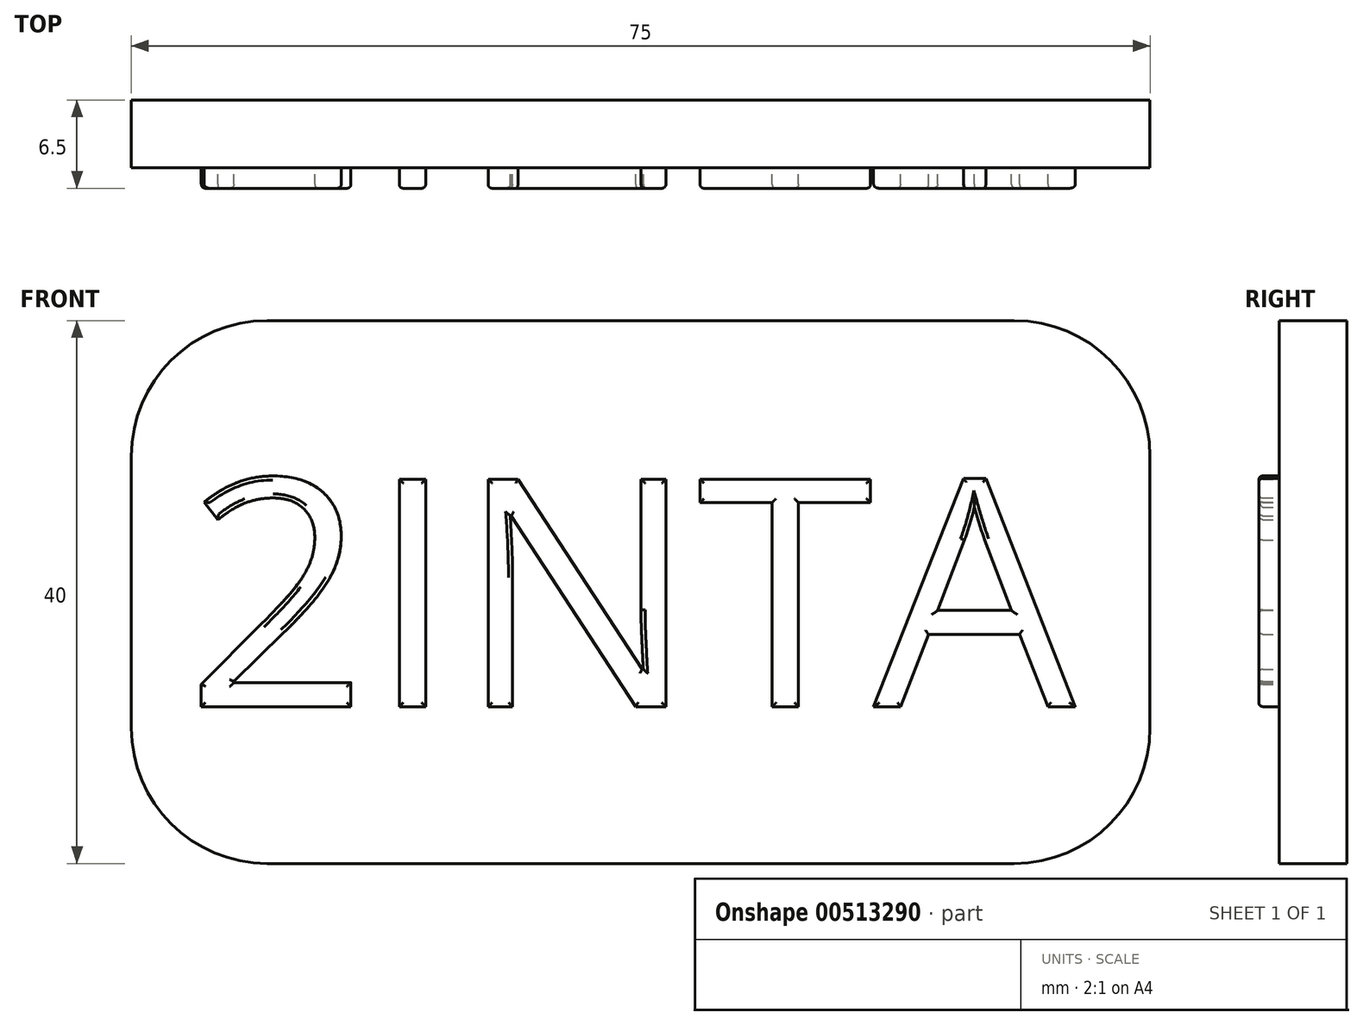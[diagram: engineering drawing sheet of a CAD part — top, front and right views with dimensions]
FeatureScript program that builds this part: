
annotation { "Feature Type Name" : "Feature", "Feature Type Description" : "" }
export const myFeature = defineFeature(function(context is Context, id is Id, definition is map)
    precondition{}
    {
        {
            var Q0;
            Q0=qCreatedBy(makeId("Front.planeOp"),FACE);
            var sketch = newSketch(context, id + "F0", { "sketchPlane" : qUnion([Q0])});
            skLineSegment(sketch, "E0.bottom", {"start": v(-67.92, -49.76) * mm, "end": v(7.08, -49.76) * mm});
            skLineSegment(sketch, "E0.top", {"start": v(-67.92, -9.76) * mm, "end": v(7.08, -9.76) * mm});
            skLineSegment(sketch, "E0.left", {"start": v(-67.92, -49.76) * mm, "end": v(-67.92, -9.76) * mm});
            skLineSegment(sketch, "E0.right", {"start": v(7.08, -49.76) * mm, "end": v(7.08, -9.76) * mm});
            skSolve(sketch);
        }
        {
            var Q0;
            Q0=makeQuery(id+"F0.imprint","IMPRINT",FACE,{"disambiguationData":[TD([[makeQuery(id+"F0.imprint","IMPRINT",EDGE,{"derivedFrom":sQuery(id+"F0.wireOp",EDGE,"E0.bottom")}),1.0]])]});
            extrude(context, id + "F1", {"entities" : qUnion([Q0]), "depth" : 5 * mm});
        }
        {
            var Q0;
            Q0=makeQuery(id+"F1.opExtrude","CAP_FACE",FACE,{"disambiguationData":[OSD([sQuery(id+"F0.wireOp",EDGE,"E0.bottom"),sQuery(id+"F0.wireOp",EDGE,"E0.top"),sQuery(id+"F0.wireOp",EDGE,"E0.left"),sQuery(id+"F0.wireOp",EDGE,"E0.right")])],"isStart":false});
            var sketch = newSketch(context, id + "F2", { "sketchPlane" : qUnion([Q0])});
            skLineSegment(sketch, "E1", {"start": v(-67.92, -49.76) * mm, "end": v(-67.92, -45.76) * mm});
            skLineSegment(sketch, "E2", {"start": v(-67.92, -45.76) * mm, "end": v(-63.92, -45.76) * mm});
            skLineSegment(sketch, "E3", {"start": v(-63.92, -45.76) * mm, "end": v(-63.92, -49.76) * mm});
            skLineSegment(sketch, "E4", {"start": v(-63.92, -49.76) * mm, "end": v(-67.92, -49.76) * mm});
            skLineSegment(sketch, "E5", {"start": v(7.08, -9.76) * mm, "end": v(3.08, -9.76) * mm});
            skLineSegment(sketch, "E6", {"start": v(3.08, -9.76) * mm, "end": v(3.08, -13.76) * mm});
            skLineSegment(sketch, "E7", {"start": v(3.08, -13.76) * mm, "end": v(7.08, -13.76) * mm});
            skLineSegment(sketch, "E8", {"start": v(7.08, -13.76) * mm, "end": v(7.08, -9.76) * mm});
            skSolve(sketch);
        }
        {
            var Q0;
            {var subQ3=sQuery(id+"F2.wireOp",EDGE,"E2");Q0=makeQuery(id+"F2.imprint","IMPRINT",FACE,{"disambiguationData":[TD([[makeQuery(id+"F2.imprint","IMPRINT",EDGE,{"derivedFrom":subQ3}),1.0]])]});}
            var sketch = newSketch(context, id + "F3", { "sketchPlane" : qUnion([Q0])});
            skText(sketch, "E9", { "text": "2INTA", "fontName": "OpenSans-Regular.ttf"});
            const initialGuessF3  = {"E9": [-0.06392, -0.0382, 1, 0, 0.0169]};
            skSetInitialGuess(sketch, initialGuessF3);
            skSolve(sketch);
        }
        {
            var Q0;
            Q0 = qSketchRegion(id + "F3", true);
            extrude(context, id + "F4", {"entities" : qUnion([Q0]), "operationType" : NewBodyOperationType.ADD, "depth" : 1.5 * mm});
        }
        {
            var Q0;
            Q0=makeQuery(id+"F1.opExtrude","SWEPT_EDGE",EDGE,{"disambiguationData":[OSD([sQuery(id+"F0.wireOp",EDGE,"E0.top"),sQuery(id+"F0.wireOp",EDGE,"E0.right")])]});
            var Q1;
            Q1=makeQuery(id+"F1.opExtrude","SWEPT_EDGE",EDGE,{"disambiguationData":[OSD([sQuery(id+"F0.wireOp",EDGE,"E0.bottom"),sQuery(id+"F0.wireOp",EDGE,"E0.right")])]});
            var Q2;
            Q2=makeQuery(id+"F1.opExtrude","SWEPT_EDGE",EDGE,{"disambiguationData":[OSD([sQuery(id+"F0.wireOp",EDGE,"E0.bottom"),sQuery(id+"F0.wireOp",EDGE,"E0.left")])]});
            var Q3;
            Q3=makeQuery(id+"F1.opExtrude","SWEPT_EDGE",EDGE,{"disambiguationData":[OSD([sQuery(id+"F0.wireOp",EDGE,"E0.top"),sQuery(id+"F0.wireOp",EDGE,"E0.left")])]});
            fillet(context, id + "F5", {"entities" : qUnion([Q0, Q1, Q2, Q3]), "radius" : 10 * mm, "tangentPropagation" : true, "allowEdgeOverflow" : false});
        }
        {
            var Q0;
            Q0=makeQuery(id+"F4.opExtrude","CAP_FACE",FACE,{"disambiguationData":[OSD([sQuery(id+"F3.wireOp",EDGE,"E9.sketch_text.stroke-0"),sQuery(id+"F3.wireOp",EDGE,"E9.sketch_text.stroke-1"),sQuery(id+"F3.wireOp",EDGE,"E9.sketch_text.stroke-2"),sQuery(id+"F3.wireOp",EDGE,"E9.sketch_text.stroke-3"),sQuery(id+"F3.wireOp",EDGE,"E9.sketch_text.stroke-4"),sQuery(id+"F3.wireOp",EDGE,"E9.sketch_text.stroke-5"),sQuery(id+"F3.wireOp",EDGE,"E9.sketch_text.stroke-6"),sQuery(id+"F3.wireOp",EDGE,"E9.sketch_text.stroke-7"),sQuery(id+"F3.wireOp",EDGE,"E9.sketch_text.stroke-8"),sQuery(id+"F3.wireOp",EDGE,"E9.sketch_text.stroke-9"),sQuery(id+"F3.wireOp",EDGE,"E9.sketch_text.stroke-10"),sQuery(id+"F3.wireOp",EDGE,"E9.sketch_text.stroke-11"),sQuery(id+"F3.wireOp",EDGE,"E9.sketch_text.stroke-12"),sQuery(id+"F3.wireOp",EDGE,"E9.sketch_text.stroke-13"),sQuery(id+"F3.wireOp",EDGE,"E9.sketch_text.stroke-14"),sQuery(id+"F3.wireOp",EDGE,"E9.sketch_text.stroke-15"),sQuery(id+"F3.wireOp",EDGE,"E9.sketch_text.stroke-16"),sQuery(id+"F3.wireOp",EDGE,"E9.sketch_text.stroke-17"),sQuery(id+"F3.wireOp",EDGE,"E9.sketch_text.stroke-18"),sQuery(id+"F3.wireOp",EDGE,"E9.sketch_text.stroke-19")])],"isStart":false});
            var Q1;
            Q1=makeQuery(id+"F4.opExtrude","CAP_FACE",FACE,{"disambiguationData":[OSD([sQuery(id+"F3.wireOp",EDGE,"E9.sketch_text.stroke-20"),sQuery(id+"F3.wireOp",EDGE,"E9.sketch_text.stroke-21"),sQuery(id+"F3.wireOp",EDGE,"E9.sketch_text.stroke-22"),sQuery(id+"F3.wireOp",EDGE,"E9.sketch_text.stroke-23")])],"isStart":false});
            var Q2;
            Q2=makeQuery(id+"F4.opExtrude","CAP_FACE",FACE,{"disambiguationData":[OSD([sQuery(id+"F3.wireOp",EDGE,"E9.sketch_text.stroke-24"),sQuery(id+"F3.wireOp",EDGE,"E9.sketch_text.stroke-25"),sQuery(id+"F3.wireOp",EDGE,"E9.sketch_text.stroke-26"),sQuery(id+"F3.wireOp",EDGE,"E9.sketch_text.stroke-27"),sQuery(id+"F3.wireOp",EDGE,"E9.sketch_text.stroke-28"),sQuery(id+"F3.wireOp",EDGE,"E9.sketch_text.stroke-29"),sQuery(id+"F3.wireOp",EDGE,"E9.sketch_text.stroke-30"),sQuery(id+"F3.wireOp",EDGE,"E9.sketch_text.stroke-31"),sQuery(id+"F3.wireOp",EDGE,"E9.sketch_text.stroke-32"),sQuery(id+"F3.wireOp",EDGE,"E9.sketch_text.stroke-33"),sQuery(id+"F3.wireOp",EDGE,"E9.sketch_text.stroke-34"),sQuery(id+"F3.wireOp",EDGE,"E9.sketch_text.stroke-35"),sQuery(id+"F3.wireOp",EDGE,"E9.sketch_text.stroke-36"),sQuery(id+"F3.wireOp",EDGE,"E9.sketch_text.stroke-37"),sQuery(id+"F3.wireOp",EDGE,"E9.sketch_text.stroke-38")])],"isStart":false});
            var Q3;
            Q3=makeQuery(id+"F4.opExtrude","CAP_FACE",FACE,{"disambiguationData":[OSD([sQuery(id+"F3.wireOp",EDGE,"E9.sketch_text.stroke-39"),sQuery(id+"F3.wireOp",EDGE,"E9.sketch_text.stroke-40"),sQuery(id+"F3.wireOp",EDGE,"E9.sketch_text.stroke-41"),sQuery(id+"F3.wireOp",EDGE,"E9.sketch_text.stroke-42"),sQuery(id+"F3.wireOp",EDGE,"E9.sketch_text.stroke-43"),sQuery(id+"F3.wireOp",EDGE,"E9.sketch_text.stroke-44"),sQuery(id+"F3.wireOp",EDGE,"E9.sketch_text.stroke-45"),sQuery(id+"F3.wireOp",EDGE,"E9.sketch_text.stroke-46")])],"isStart":false});
            var Q4;
            Q4=makeQuery(id+"F4.opExtrude","CAP_FACE",FACE,{"disambiguationData":[OSD([sQuery(id+"F3.wireOp",EDGE,"E9.sketch_text.stroke-47"),sQuery(id+"F3.wireOp",EDGE,"E9.sketch_text.stroke-48"),sQuery(id+"F3.wireOp",EDGE,"E9.sketch_text.stroke-49"),sQuery(id+"F3.wireOp",EDGE,"E9.sketch_text.stroke-50"),sQuery(id+"F3.wireOp",EDGE,"E9.sketch_text.stroke-51"),sQuery(id+"F3.wireOp",EDGE,"E9.sketch_text.stroke-52"),sQuery(id+"F3.wireOp",EDGE,"E9.sketch_text.stroke-53"),sQuery(id+"F3.wireOp",EDGE,"E9.sketch_text.stroke-54"),sQuery(id+"F3.wireOp",EDGE,"E9.sketch_text.stroke-55"),sQuery(id+"F3.wireOp",EDGE,"E9.sketch_text.stroke-56"),sQuery(id+"F3.wireOp",EDGE,"E9.sketch_text.stroke-57"),sQuery(id+"F3.wireOp",EDGE,"E9.sketch_text.stroke-58"),sQuery(id+"F3.wireOp",EDGE,"E9.sketch_text.stroke-59")])],"isStart":false});
            fillet(context, id + "F6", {"entities" : qUnion([Q0, Q1, Q2, Q3, Q4]), "radius" : 0.3 * mm, "tangentPropagation" : true, "allowEdgeOverflow" : false});
        }
    });
